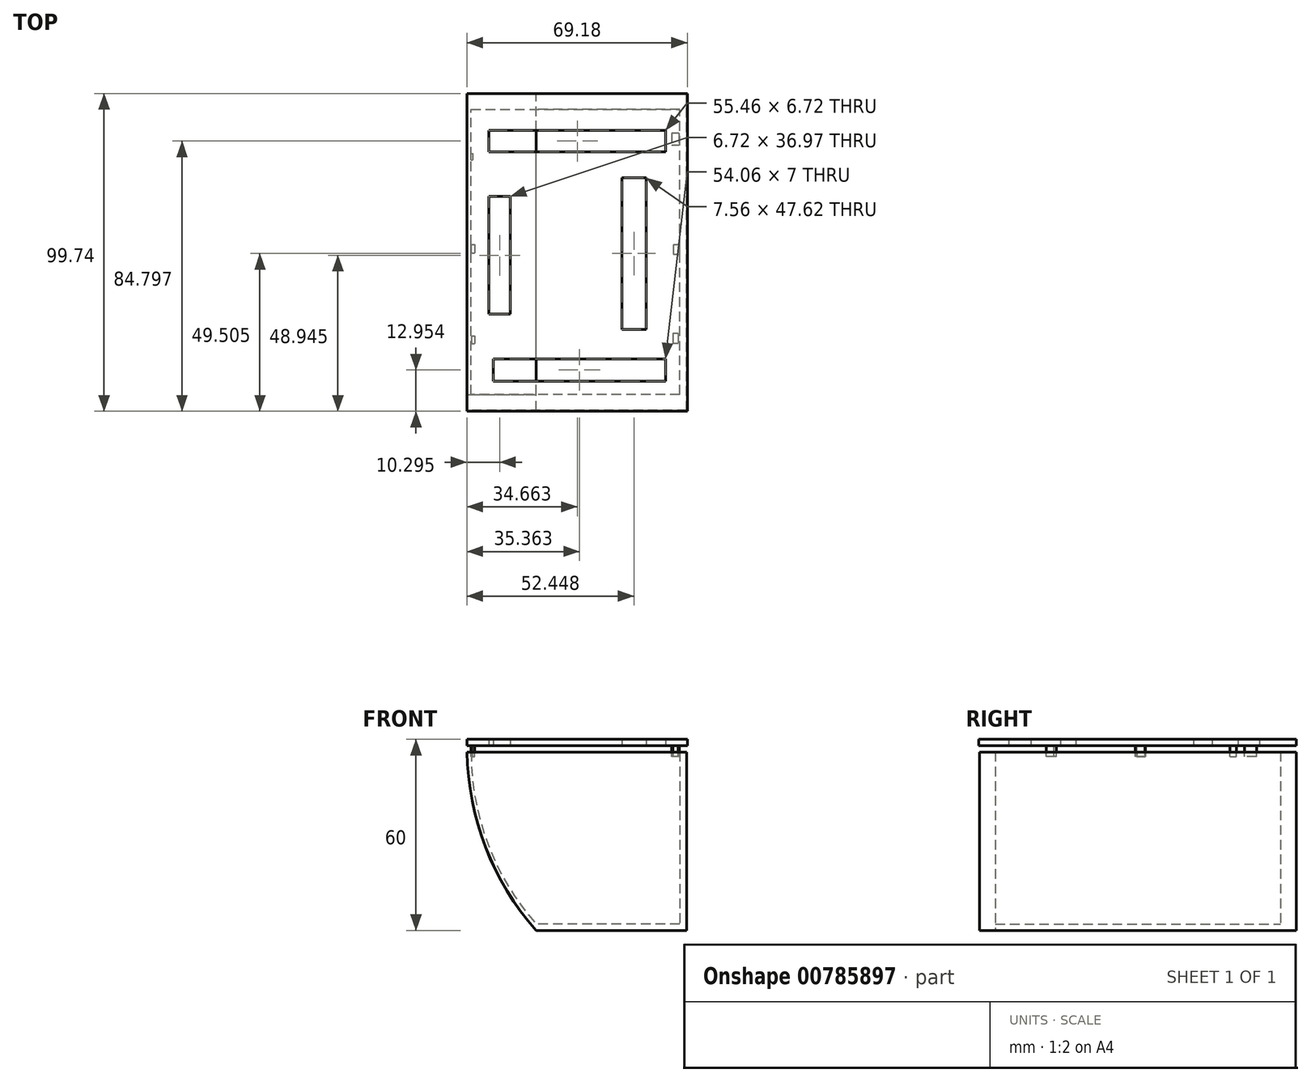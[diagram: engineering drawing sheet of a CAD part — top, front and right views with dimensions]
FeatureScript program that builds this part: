
annotation { "Feature Type Name" : "Feature", "Feature Type Description" : "" }
export const myFeature = defineFeature(function(context is Context, id is Id, definition is map)
    precondition{}
    {
        {
            var Q0;
            Q0=qCreatedBy(makeId("Front.planeOp"),FACE);
            var sketch = newSketch(context, id + "F0", { "sketchPlane" : qUnion([Q0])});
            skLineSegment(sketch, "E0", {"start": v(-88.54, 0) * mm, "end": v(-19.54, 0) * mm});
            skLineSegment(sketch, "E1", {"start": v(-19.54, 0) * mm, "end": v(-19.54, -58) * mm});
            skLineSegment(sketch, "E2", {"start": v(-19.54, -58) * mm, "end": v(-66.9, -58) * mm});
            skArc(sketch, "E3", {"start": v(-88.54, 0) * mm, "mid": v(-83.07, -31) * mm, "end": v(-66.9, -58) * mm});
            skLineSegment(sketch, "E4", {"start": v(-66.9, -58) * mm, "end": v(-66.9, -56) * mm});
            skLineSegment(sketch, "E5", {"start": v(-19.54, -56) * mm, "end": v(-66.9, -56) * mm});
            skLineSegment(sketch, "E6", {"start": v(-66.9, 0) * mm, "end": v(-66.9, -2) * mm});
            skLineSegment(sketch, "E7", {"start": v(-66.9, -2) * mm, "end": v(-19.54, -2) * mm});
            skLineSegment(sketch, "E8", {"start": v(-21.76, -2) * mm, "end": v(-21.76, -56) * mm});
            skLineSegment(sketch, "E9", {"start": v(-66.9, -2) * mm, "end": v(-88.53, -2) * mm});
            skPoint(sketch, "E10", {"position": v(-87.26, 0) * mm});
            skArc(sketch, "E11", {"start": v(-87.26, 0) * mm, "mid": v(-82.33, -29.91) * mm, "end": v(-66.9, -56) * mm});
            skSolve(sketch);
        }
        {
            var Q0;
            {var subQ0=sQuery(id+"F0.wireOp",EDGE,"E4");Q0=makeQuery(id+"F0.imprint","IMPRINT",FACE,{"disambiguationData":[TD([[makeQuery(id+"F0.imprint","IMPRINT",EDGE,{"derivedFrom":subQ0}),1.0]])]});}
            var Q1;
            {var subQ1=sQuery(id+"F0.wireOp",EDGE,"E2");Q1=makeQuery(id+"F0.imprint","IMPRINT",FACE,{"disambiguationData":[TD([[makeQuery(id+"F0.imprint","IMPRINT",EDGE,{"derivedFrom":subQ1}),-1.0]])]});}
            var Q2;
            {var subQ5=sQuery(id+"F0.wireOp",EDGE,"E8");Q2=makeQuery(id+"F0.imprint","IMPRINT",FACE,{"disambiguationData":[TD([[makeQuery(id+"F0.imprint","IMPRINT",EDGE,{"derivedFrom":subQ5}),1.0]])]});}
            var Q3;
            Q3=sQuery(id+"F0.wireOp",EDGE,"E2");
            var Q4;
            Q4=sQuery(id+"F0.wireOp",EDGE,"E5");
            var Q5;
            Q5=sQuery(id+"F0.wireOp",EDGE,"E1");
            var Q6;
            Q6=sQuery(id+"F0.wireOp",EDGE,"E8");
            var Q7;
            Q7=sQuery(id+"F0.wireOp",EDGE,"E3");
            var Q8;
            Q8=sQuery(id+"F0.wireOp",EDGE,"E11");
            extrude(context, id + "F1", {"entities" : qUnion([Q0, Q1, Q2]), "surfaceEntities" : qUnion([Q3, Q4, Q5, Q6, Q7, Q8]), "depth" : 89.5 * mm, "offsetDistance" : 25 * mm});
        }
        {
            var Q0;
            {var subQ0=sQuery(id+"F0.wireOp",EDGE,"E8");Q0=makeQuery(id+"F0.imprint","IMPRINT",FACE,{"disambiguationData":[TD([[makeQuery(id+"F0.imprint","IMPRINT",EDGE,{"derivedFrom":subQ0}),-1.0]])]});}
            var Q1;
            Q1=makeQuery(id+"F1.opExtrude","CAP_FACE",FACE,{"disambiguationData":[OSD([sQuery(id+"F0.wireOp",EDGE,"E1"),sQuery(id+"F0.wireOp",EDGE,"E2"),sQuery(id+"F0.wireOp",EDGE,"E3"),sQuery(id+"F0.wireOp",EDGE,"E5"),sQuery(id+"F0.wireOp",EDGE,"E7"),sQuery(id+"F0.wireOp",EDGE,"E8"),sQuery(id+"F0.wireOp",EDGE,"E9"),sQuery(id+"F0.wireOp",EDGE,"E11")])],"isStart":true});
            extrude(context, id + "F2", {"entities" : qUnion([Q0, Q1]), "operationType" : NewBodyOperationType.ADD, "oppositeDirection" : true, "depth" : 5 * mm, "offsetDistance" : 25 * mm});
        }
        {
            var Q0;
            Q0=makeQuery(id+"F1.opExtrude","CAP_FACE",FACE,{"disambiguationData":[OSD([sQuery(id+"F0.wireOp",EDGE,"E1"),sQuery(id+"F0.wireOp",EDGE,"E2"),sQuery(id+"F0.wireOp",EDGE,"E3"),sQuery(id+"F0.wireOp",EDGE,"E5"),sQuery(id+"F0.wireOp",EDGE,"E7"),sQuery(id+"F0.wireOp",EDGE,"E8"),sQuery(id+"F0.wireOp",EDGE,"E9"),sQuery(id+"F0.wireOp",EDGE,"E11")])],"isStart":false});
            var sketch = newSketch(context, id + "F3", { "sketchPlane" : qUnion([Q0])});
            skLineSegment(sketch, "E12", {"start": v(-66.9, -58) * mm, "end": v(-19.54, -58) * mm});
            skLineSegment(sketch, "E13", {"start": v(-19.54, -58) * mm, "end": v(-19.54, -2) * mm});
            skLineSegment(sketch, "E14", {"start": v(-19.54, -2) * mm, "end": v(-88.53, -2) * mm});
            skArc(sketch, "E15", {"start": v(-88.53, -2) * mm, "mid": v(-82.7, -31.92) * mm, "end": v(-66.9, -58) * mm});
            skSolve(sketch);
        }
        {
            var Q0;
            Q0 = qSketchRegion(id + "F3", true);
            extrude(context, id + "F4", {"entities" : qUnion([Q0]), "operationType" : NewBodyOperationType.ADD, "depth" : 5 * mm, "offsetDistance" : 25 * mm});
        }
        {
            var Q0;
            Q0=qCreatedBy(makeId("Top.planeOp"),FACE);
            var sketch = newSketch(context, id + "F5", { "sketchPlane" : qUnion([Q0])});
            skLineSegment(sketch, "E16.bottom", {"start": v(-19.4, 4.97) * mm, "end": v(-88.58, 4.97) * mm});
            skLineSegment(sketch, "E16.top", {"start": v(-19.4, -94.74) * mm, "end": v(-88.58, -94.74) * mm});
            skLineSegment(sketch, "E16.left", {"start": v(-19.4, 4.97) * mm, "end": v(-19.4, -94.74) * mm});
            skLineSegment(sketch, "E16.right", {"start": v(-88.58, 4.97) * mm, "end": v(-88.58, -94.74) * mm});
            skLineSegment(sketch, "E17.bottom", {"start": v(-81.65, -6.58) * mm, "end": v(-26.19, -6.58) * mm});
            skLineSegment(sketch, "E17.top", {"start": v(-81.65, -13.3) * mm, "end": v(-26.19, -13.3) * mm});
            skLineSegment(sketch, "E17.left", {"start": v(-81.65, -6.58) * mm, "end": v(-81.65, -13.3) * mm});
            skLineSegment(sketch, "E17.right", {"start": v(-26.19, -6.58) * mm, "end": v(-26.19, -13.3) * mm});
            skLineSegment(sketch, "E18.bottom", {"start": v(-81.65, -27.3) * mm, "end": v(-74.92, -27.3) * mm});
            skLineSegment(sketch, "E18.top", {"start": v(-81.65, -64.28) * mm, "end": v(-74.92, -64.28) * mm});
            skLineSegment(sketch, "E18.left", {"start": v(-81.65, -27.3) * mm, "end": v(-81.65, -64.28) * mm});
            skLineSegment(sketch, "E18.right", {"start": v(-74.92, -27.3) * mm, "end": v(-74.92, -64.28) * mm});
            skLineSegment(sketch, "E19.bottom", {"start": v(-80.25, -78.29) * mm, "end": v(-26.19, -78.29) * mm});
            skLineSegment(sketch, "E19.top", {"start": v(-80.25, -85.29) * mm, "end": v(-26.19, -85.29) * mm});
            skLineSegment(sketch, "E19.left", {"start": v(-80.25, -78.29) * mm, "end": v(-80.25, -85.29) * mm});
            skLineSegment(sketch, "E19.right", {"start": v(-26.19, -78.29) * mm, "end": v(-26.19, -85.29) * mm});
            skLineSegment(sketch, "E20.bottom", {"start": v(-32.35, -21.43) * mm, "end": v(-39.91, -21.43) * mm});
            skLineSegment(sketch, "E20.top", {"start": v(-32.35, -69.04) * mm, "end": v(-39.91, -69.04) * mm});
            skLineSegment(sketch, "E20.left", {"start": v(-32.35, -21.43) * mm, "end": v(-32.35, -69.04) * mm});
            skLineSegment(sketch, "E20.right", {"start": v(-39.91, -21.43) * mm, "end": v(-39.91, -69.04) * mm});
            skLineSegment(sketch, "E21.bottom", {"start": v(-21.96, -18.63) * mm, "end": v(-23.1, -18.63) * mm});
            skLineSegment(sketch, "E21.top", {"start": v(-21.96, -22.9) * mm, "end": v(-23.1, -22.9) * mm});
            skLineSegment(sketch, "E21.left", {"start": v(-21.96, -18.63) * mm, "end": v(-21.96, -22.9) * mm});
            skLineSegment(sketch, "E21.right", {"start": v(-23.1, -18.63) * mm, "end": v(-23.1, -22.9) * mm});
            skLineSegment(sketch, "E22.bottom", {"start": v(-21.61, -57.59) * mm, "end": v(-23.1, -57.59) * mm});
            skLineSegment(sketch, "E22.top", {"start": v(-21.61, -61.58) * mm, "end": v(-23.1, -61.58) * mm});
            skLineSegment(sketch, "E22.left", {"start": v(-21.61, -57.59) * mm, "end": v(-21.61, -61.58) * mm});
            skLineSegment(sketch, "E22.right", {"start": v(-23.1, -57.59) * mm, "end": v(-23.1, -61.58) * mm});
            skLineSegment(sketch, "E23.bottom", {"start": v(-86.99, -18.16) * mm, "end": v(-85.37, -18.16) * mm});
            skLineSegment(sketch, "E23.top", {"start": v(-86.99, -21.78) * mm, "end": v(-85.37, -21.78) * mm});
            skLineSegment(sketch, "E23.left", {"start": v(-86.99, -18.16) * mm, "end": v(-86.99, -21.78) * mm});
            skLineSegment(sketch, "E23.right", {"start": v(-85.37, -18.16) * mm, "end": v(-85.37, -21.78) * mm});
            skLineSegment(sketch, "E24.bottom", {"start": v(-86.99, -70.06) * mm, "end": v(-85.62, -70.06) * mm});
            skLineSegment(sketch, "E24.top", {"start": v(-86.99, -73.93) * mm, "end": v(-85.62, -73.93) * mm});
            skLineSegment(sketch, "E24.left", {"start": v(-86.99, -70.06) * mm, "end": v(-86.99, -73.93) * mm});
            skLineSegment(sketch, "E24.right", {"start": v(-85.62, -70.06) * mm, "end": v(-85.62, -73.93) * mm});
            skSolve(sketch);
        }
        {
            var Q0;
            Q0=makeQuery(id+"F5.imprint","IMPRINT",FACE,{"disambiguationData":[TD([[makeQuery(id+"F5.imprint","IMPRINT",EDGE,{"derivedFrom":sQuery(id+"F5.wireOp",EDGE,"E16.bottom")}),1.0]])]});
            var Q1;
            Q1=makeQuery(id+"F5.imprint","IMPRINT",FACE,{"disambiguationData":[TD([[makeQuery(id+"F5.imprint","IMPRINT",EDGE,{"derivedFrom":sQuery(id+"F5.wireOp",EDGE,"E24.bottom")}),-1.0]])]});
            var Q2;
            Q2=makeQuery(id+"F5.imprint","IMPRINT",FACE,{"disambiguationData":[TD([[makeQuery(id+"F5.imprint","IMPRINT",EDGE,{"derivedFrom":sQuery(id+"F5.wireOp",EDGE,"E23.bottom")}),-1.0]])]});
            var Q3;
            Q3=makeQuery(id+"F5.imprint","IMPRINT",FACE,{"disambiguationData":[TD([[makeQuery(id+"F5.imprint","IMPRINT",EDGE,{"derivedFrom":sQuery(id+"F5.wireOp",EDGE,"E21.bottom")}),1.0]])]});
            var Q4;
            Q4=makeQuery(id+"F5.imprint","IMPRINT",FACE,{"disambiguationData":[TD([[makeQuery(id+"F5.imprint","IMPRINT",EDGE,{"derivedFrom":sQuery(id+"F5.wireOp",EDGE,"E22.bottom")}),1.0]])]});
            extrude(context, id + "F6", {"entities" : qUnion([Q0, Q1, Q2, Q3, Q4]), "depth" : 2 * mm, "offsetDistance" : 25 * mm});
        }
        {
            var Q0;
            Q0=makeQuery(id+"F6.opExtrude","CAP_FACE",FACE,{"disambiguationData":[OSD([sQuery(id+"F5.wireOp",EDGE,"E16.bottom"),sQuery(id+"F5.wireOp",EDGE,"E16.top"),sQuery(id+"F5.wireOp",EDGE,"E16.left"),sQuery(id+"F5.wireOp",EDGE,"E16.right"),sQuery(id+"F5.wireOp",EDGE,"E17.bottom"),sQuery(id+"F5.wireOp",EDGE,"E17.top"),sQuery(id+"F5.wireOp",EDGE,"E17.left"),sQuery(id+"F5.wireOp",EDGE,"E17.right"),sQuery(id+"F5.wireOp",EDGE,"E18.bottom"),sQuery(id+"F5.wireOp",EDGE,"E18.top"),sQuery(id+"F5.wireOp",EDGE,"E18.left"),sQuery(id+"F5.wireOp",EDGE,"E18.right"),sQuery(id+"F5.wireOp",EDGE,"E19.bottom"),sQuery(id+"F5.wireOp",EDGE,"E19.top"),sQuery(id+"F5.wireOp",EDGE,"E19.left"),sQuery(id+"F5.wireOp",EDGE,"E19.right"),sQuery(id+"F5.wireOp",EDGE,"E20.bottom"),sQuery(id+"F5.wireOp",EDGE,"E20.top"),sQuery(id+"F5.wireOp",EDGE,"E20.left"),sQuery(id+"F5.wireOp",EDGE,"E20.right")])],"isStart":false});
            var sketch = newSketch(context, id + "F7", { "sketchPlane" : qUnion([Q0])});
            skLineSegment(sketch, "E25.bottom", {"start": v(-87.21, -71.1) * mm, "end": v(-86.17, -71.1) * mm});
            skLineSegment(sketch, "E25.top", {"start": v(-87.21, -73.48) * mm, "end": v(-86.17, -73.48) * mm});
            skLineSegment(sketch, "E25.left", {"start": v(-87.21, -71.1) * mm, "end": v(-87.21, -73.48) * mm});
            skLineSegment(sketch, "E25.right", {"start": v(-86.17, -71.1) * mm, "end": v(-86.17, -73.48) * mm});
            skLineSegment(sketch, "E26.bottom", {"start": v(-87.28, -42.4) * mm, "end": v(-86.17, -42.4) * mm});
            skLineSegment(sketch, "E26.top", {"start": v(-87.28, -45.07) * mm, "end": v(-86.17, -45.07) * mm});
            skLineSegment(sketch, "E26.left", {"start": v(-87.28, -42.4) * mm, "end": v(-87.28, -45.07) * mm});
            skLineSegment(sketch, "E26.right", {"start": v(-86.17, -42.4) * mm, "end": v(-86.17, -45.07) * mm});
            skLineSegment(sketch, "E27.bottom", {"start": v(-21.92, -42.48) * mm, "end": v(-23.82, -42.48) * mm});
            skLineSegment(sketch, "E27.top", {"start": v(-21.92, -45.57) * mm, "end": v(-23.82, -45.57) * mm});
            skLineSegment(sketch, "E27.left", {"start": v(-21.92, -42.48) * mm, "end": v(-21.92, -45.57) * mm});
            skLineSegment(sketch, "E27.right", {"start": v(-23.82, -42.48) * mm, "end": v(-23.82, -45.57) * mm});
            skLineSegment(sketch, "E28.bottom", {"start": v(-22.27, -70.37) * mm, "end": v(-23.94, -70.37) * mm});
            skLineSegment(sketch, "E28.top", {"start": v(-22.27, -73.48) * mm, "end": v(-23.94, -73.48) * mm});
            skLineSegment(sketch, "E28.left", {"start": v(-22.27, -70.37) * mm, "end": v(-22.27, -73.48) * mm});
            skLineSegment(sketch, "E28.right", {"start": v(-23.94, -70.37) * mm, "end": v(-23.94, -73.48) * mm});
            skLineSegment(sketch, "E29.bottom", {"start": v(-22.04, -7.48) * mm, "end": v(-24.3, -7.48) * mm});
            skLineSegment(sketch, "E29.top", {"start": v(-22.04, -11.27) * mm, "end": v(-24.3, -11.27) * mm});
            skLineSegment(sketch, "E29.left", {"start": v(-22.04, -7.48) * mm, "end": v(-22.04, -11.27) * mm});
            skLineSegment(sketch, "E29.right", {"start": v(-24.3, -7.48) * mm, "end": v(-24.3, -11.27) * mm});
            skLineSegment(sketch, "E30.bottom", {"start": v(-87.27, -13.86) * mm, "end": v(-86.73, -13.86) * mm});
            skLineSegment(sketch, "E30.top", {"start": v(-87.27, -15.8) * mm, "end": v(-86.73, -15.8) * mm});
            skLineSegment(sketch, "E30.left", {"start": v(-87.27, -13.86) * mm, "end": v(-87.27, -15.8) * mm});
            skLineSegment(sketch, "E30.right", {"start": v(-86.73, -13.86) * mm, "end": v(-86.73, -15.8) * mm});
            skSolve(sketch);
        }
        {
            var Q0;
            Q0 = qSketchRegion(id + "F7", true);
            extrude(context, id + "F8", {"entities" : qUnion([Q0]), "operationType" : NewBodyOperationType.ADD, "oppositeDirection" : true, "depth" : 5.5 * mm, "offsetDistance" : 25 * mm});
        }
    });
